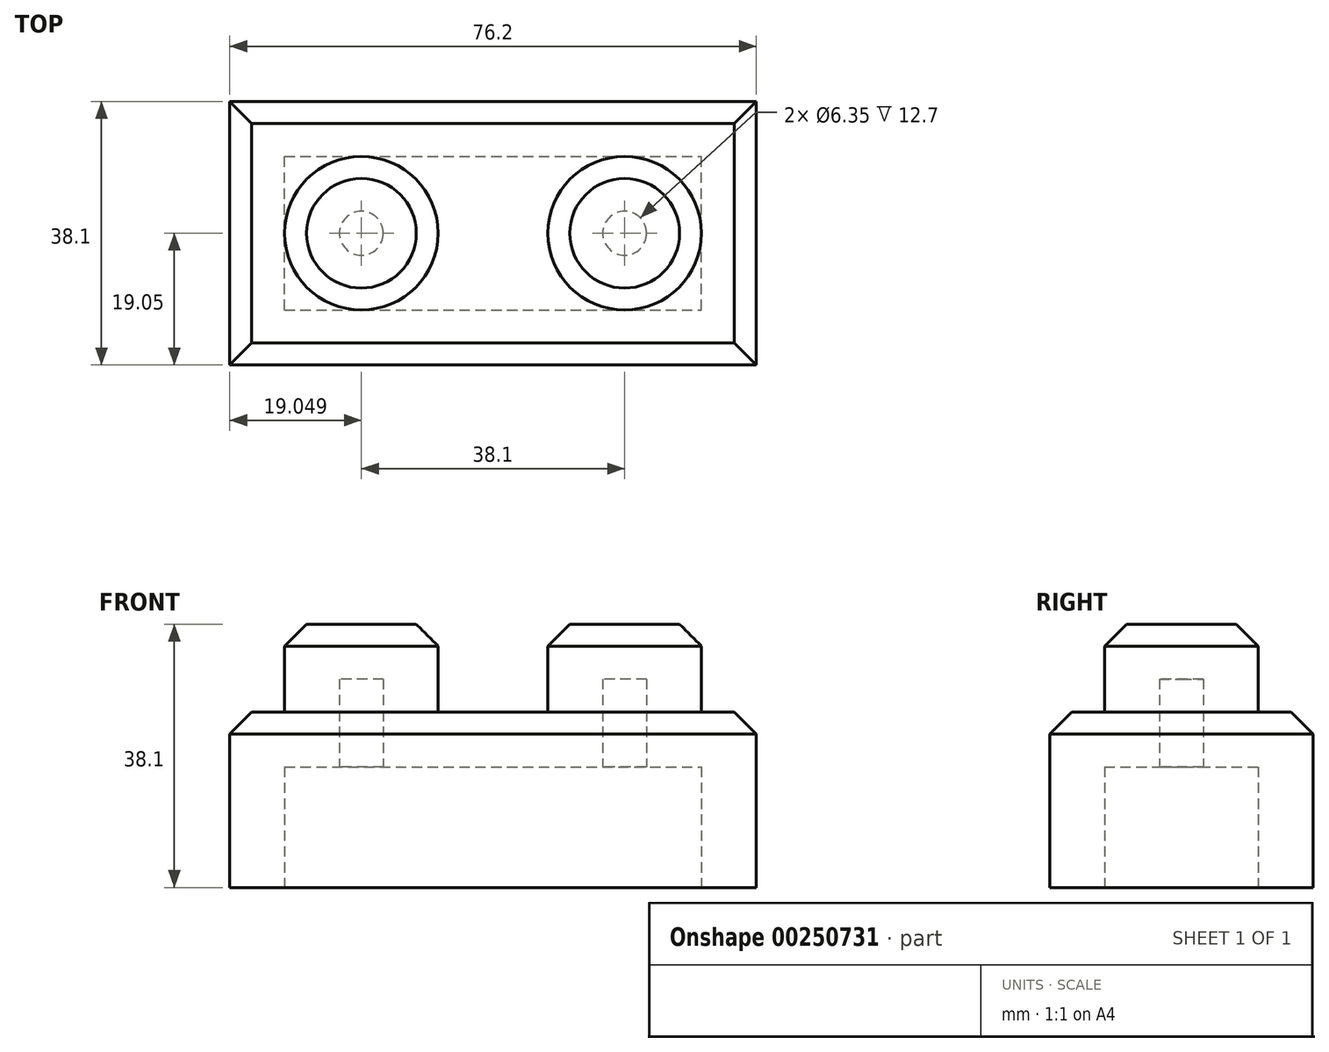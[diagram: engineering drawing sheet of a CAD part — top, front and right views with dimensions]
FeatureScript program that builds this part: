
annotation { "Feature Type Name" : "Feature", "Feature Type Description" : "" }
export const myFeature = defineFeature(function(context is Context, id is Id, definition is map)
    precondition{}
    {
        {
            var Q0;
            Q0=qCreatedBy(makeId("Top.planeOp"),FACE);
            var sketch = newSketch(context, id + "F0", { "sketchPlane" : qUnion([Q0])});
            skLineSegment(sketch, "E0.bottom", {"start": v(-9.71, 0) * mm, "end": v(66.49, 0) * mm});
            skLineSegment(sketch, "E0.top", {"start": v(-9.71, 38.1) * mm, "end": v(66.49, 38.1) * mm});
            skLineSegment(sketch, "E0.left", {"start": v(-9.71, 0) * mm, "end": v(-9.71, 38.1) * mm});
            skLineSegment(sketch, "E0.right", {"start": v(66.49, 0) * mm, "end": v(66.49, 38.1) * mm});
            skSolve(sketch);
        }
        {
            var Q0;
            Q0=makeQuery(id+"F0.imprint","IMPRINT",FACE,{"disambiguationData":[TD([[makeQuery(id+"F0.imprint","IMPRINT",EDGE,{"derivedFrom":sQuery(id+"F0.wireOp",EDGE,"E0.bottom")}),1.0]])]});
            extrude(context, id + "F1", {"entities" : qUnion([Q0]), "depth" : 25.4 * mm});
        }
        {
            var Q0;
            Q0=makeQuery(id+"F1.opExtrude","CAP_FACE",FACE,{"disambiguationData":[OSD([sQuery(id+"F0.wireOp",EDGE,"E0.bottom"),sQuery(id+"F0.wireOp",EDGE,"E0.top"),sQuery(id+"F0.wireOp",EDGE,"E0.left"),sQuery(id+"F0.wireOp",EDGE,"E0.right")])],"isStart":false});
            var sketch = newSketch(context, id + "F2", { "sketchPlane" : qUnion([Q0])});
            skCircle(sketch, "E1", {"center": v(9.34, 19.05) * mm, "radius": 11.11 * mm});
            skCircle(sketch, "E2", {"center": v(47.44, 19.05) * mm, "radius": 11.11 * mm});
            skSolve(sketch);
        }
        {
            var Q0;
            Q0=makeQuery(id+"F2.imprint","IMPRINT",FACE,{"disambiguationData":[TD([[makeQuery(id+"F2.imprint","IMPRINT",EDGE,{"derivedFrom":sQuery(id+"F2.wireOp",EDGE,"E2")}),1.0]])]});
            var Q1;
            Q1=makeQuery(id+"F2.imprint","IMPRINT",FACE,{"disambiguationData":[TD([[makeQuery(id+"F2.imprint","IMPRINT",EDGE,{"derivedFrom":sQuery(id+"F2.wireOp",EDGE,"E1")}),1.0]])]});
            extrude(context, id + "F3", {"entities" : qUnion([Q0, Q1]), "operationType" : NewBodyOperationType.ADD, "depth" : 12.7 * mm});
        }
        {
            var Q0;
            Q0=makeQuery(id+"F1.opExtrude","CAP_FACE",FACE,{"disambiguationData":[OSD([sQuery(id+"F0.wireOp",EDGE,"E0.bottom"),sQuery(id+"F0.wireOp",EDGE,"E0.top"),sQuery(id+"F0.wireOp",EDGE,"E0.left"),sQuery(id+"F0.wireOp",EDGE,"E0.right")])],"isStart":true});
            shell(context, id + "F4", {"entities" : qUnion([Q0]), "thickness" : 7.94 * mm});
        }
        {
            var Q0;
            Q0=makeQuery(id+"F3.opExtrude","CAP_FACE",FACE,{"disambiguationData":[OSD([sQuery(id+"F2.wireOp",EDGE,"E1")])],"isStart":false});
            var Q1;
            Q1=makeQuery(id+"F3.opExtrude","CAP_FACE",FACE,{"disambiguationData":[OSD([sQuery(id+"F2.wireOp",EDGE,"E2")])],"isStart":false});
            var Q2;
            Q2=makeQuery(id+"F1.opExtrude","CAP_EDGE",EDGE,{"disambiguationData":[OSD([sQuery(id+"F0.wireOp",EDGE,"E0.bottom")])],"isStart":false});
            var Q3;
            Q3=makeQuery(id+"F1.opExtrude","CAP_EDGE",EDGE,{"disambiguationData":[OSD([sQuery(id+"F0.wireOp",EDGE,"E0.right")])],"isStart":false});
            var Q4;
            Q4=makeQuery(id+"F1.opExtrude","CAP_EDGE",EDGE,{"disambiguationData":[OSD([sQuery(id+"F0.wireOp",EDGE,"E0.top")])],"isStart":false});
            var Q5;
            Q5=makeQuery(id+"F1.opExtrude","CAP_EDGE",EDGE,{"disambiguationData":[OSD([sQuery(id+"F0.wireOp",EDGE,"E0.left")])],"isStart":false});
            chamfer(context, id + "F5", {"entities" : qUnion([Q0, Q1, Q2, Q3, Q4, Q5]), "chamferType" : ChamferType.OFFSET_ANGLE, "width" : 3.17 * mm, "oppositeDirection" : false, "angle" : 45 * degree, "tangentPropagation" : true});
        }
    });
